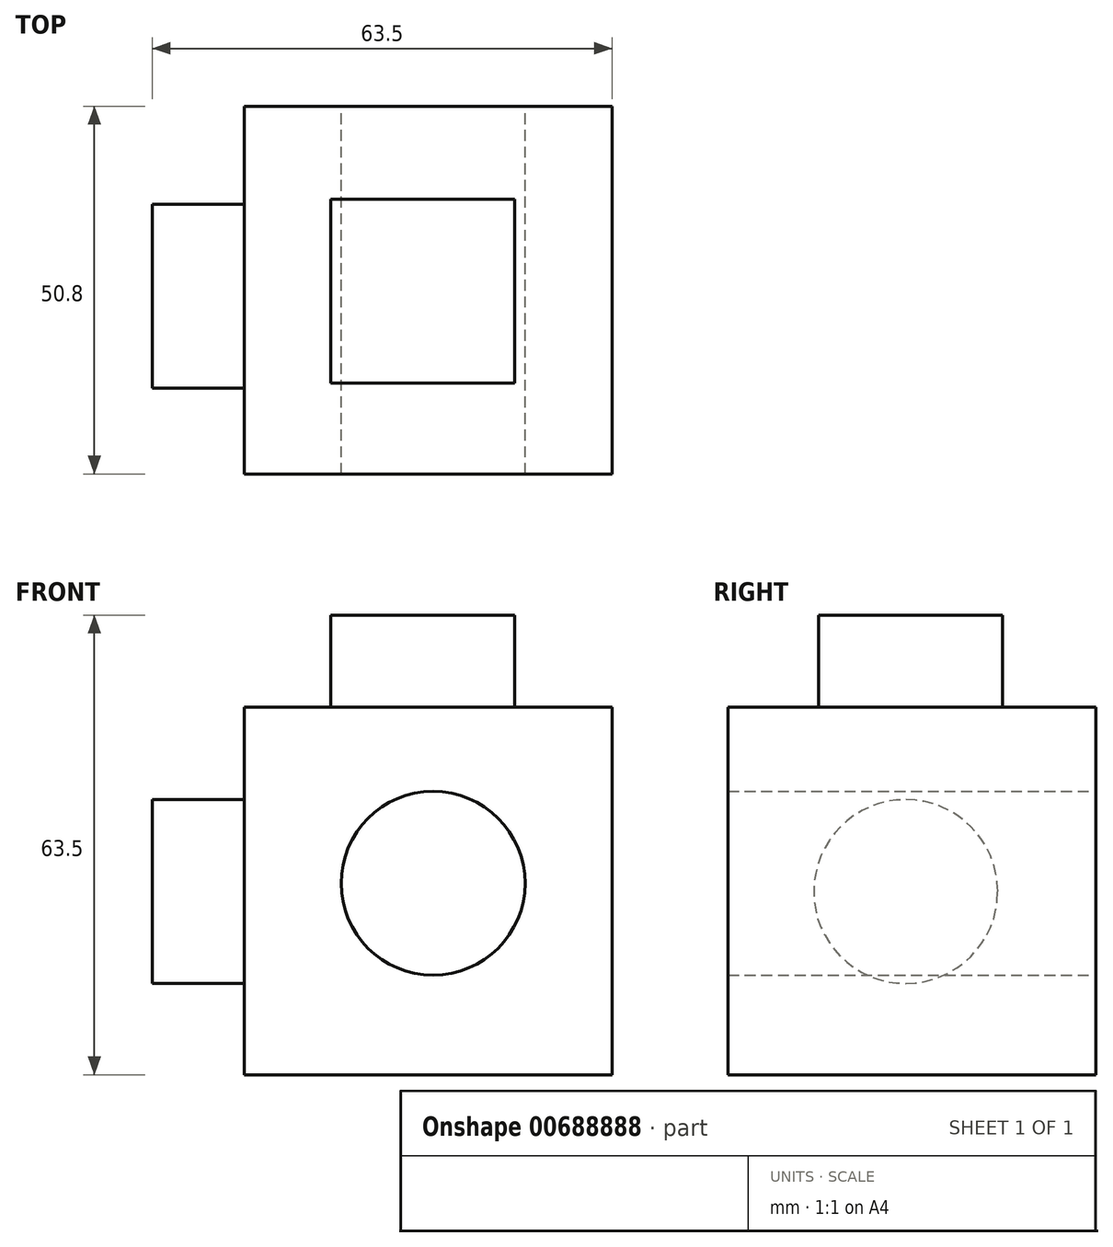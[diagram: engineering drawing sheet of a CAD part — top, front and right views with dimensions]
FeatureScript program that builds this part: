
annotation { "Feature Type Name" : "Feature", "Feature Type Description" : "" }
export const myFeature = defineFeature(function(context is Context, id is Id, definition is map)
    precondition{}
    {
        {
            var Q0;
            Q0=qCreatedBy(makeId("Front.planeOp"),FACE);
            var sketch = newSketch(context, id + "F0", { "sketchPlane" : qUnion([Q0])});
            skLineSegment(sketch, "E0.bottom", {"start": v(0, 0) * mm, "end": v(-50.8, 0) * mm});
            skLineSegment(sketch, "E0.top", {"start": v(0, 50.8) * mm, "end": v(-50.8, 50.8) * mm});
            skLineSegment(sketch, "E0.left", {"start": v(0, 0) * mm, "end": v(0, 50.8) * mm});
            skLineSegment(sketch, "E0.right", {"start": v(-50.8, 0) * mm, "end": v(-50.8, 50.8) * mm});
            skCircle(sketch, "E1", {"center": v(-24.73, 26.45) * mm, "radius": 12.7 * mm});
            skSolve(sketch);
        }
        {
            var Q0;
            Q0=makeQuery(id+"F0.imprint","IMPRINT",FACE,{"disambiguationData":[TD([[makeQuery(id+"F0.imprint","IMPRINT",EDGE,{"derivedFrom":sQuery(id+"F0.wireOp",EDGE,"E0.bottom")}),-1.0]])]});
            extrude(context, id + "F1", {"entities" : qUnion([Q0]), "depth" : 50.8 * mm, "offsetDistance" : 25.4 * mm});
        }
        {
            var Q0;
            Q0=makeQuery(id+"F1.opExtrude","SWEPT_FACE",FACE,{"disambiguationData":[OSD([sQuery(id+"F0.wireOp",EDGE,"E0.right")])]});
            var sketch = newSketch(context, id + "F2", { "sketchPlane" : qUnion([Q0])});
            skCircle(sketch, "E2", {"center": v(26.26, 25.3) * mm, "radius": 12.7 * mm});
            skSolve(sketch);
        }
        {
            var Q0;
            Q0 = qSketchRegion(id + "F2", true);
            extrude(context, id + "F3", {"entities" : qUnion([Q0]), "operationType" : NewBodyOperationType.ADD, "depth" : 12.7 * mm, "offsetDistance" : 25.4 * mm});
        }
        {
            var Q0;
            Q0=makeQuery(id+"F1.opExtrude","SWEPT_FACE",FACE,{"disambiguationData":[OSD([sQuery(id+"F0.wireOp",EDGE,"E0.top")])]});
            var sketch = newSketch(context, id + "F4", { "sketchPlane" : qUnion([Q0])});
            skLineSegment(sketch, "E3.bottom", {"start": v(-38.86, -12.89) * mm, "end": v(-13.46, -12.89) * mm});
            skLineSegment(sketch, "E3.top", {"start": v(-38.86, -38.29) * mm, "end": v(-13.46, -38.29) * mm});
            skLineSegment(sketch, "E3.left", {"start": v(-38.86, -12.89) * mm, "end": v(-38.86, -38.29) * mm});
            skLineSegment(sketch, "E3.right", {"start": v(-13.46, -12.89) * mm, "end": v(-13.46, -38.29) * mm});
            skPoint(sketch, "E3.middle", {"position": v(-26.16, -25.59) * mm});
            skSolve(sketch);
        }
        {
            var Q0;
            Q0 = qSketchRegion(id + "F4", true);
            extrude(context, id + "F5", {"entities" : qUnion([Q0]), "operationType" : NewBodyOperationType.ADD, "depth" : 12.7 * mm, "offsetDistance" : 25.4 * mm});
        }
    });
